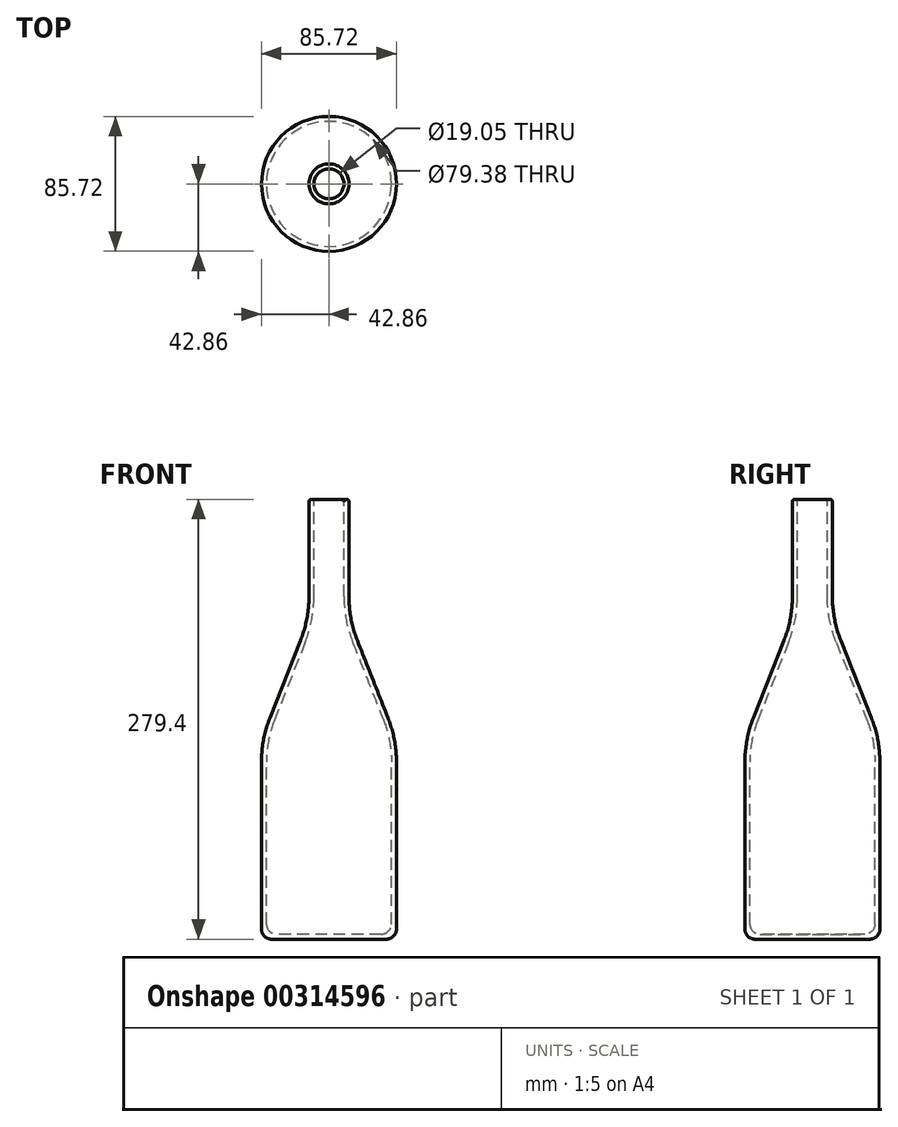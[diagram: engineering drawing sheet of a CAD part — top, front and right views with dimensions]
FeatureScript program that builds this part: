
annotation { "Feature Type Name" : "Feature", "Feature Type Description" : "" }
export const myFeature = defineFeature(function(context is Context, id is Id, definition is map)
    precondition{}
    {
        {
            var Q0;
            Q0=qCreatedBy(makeId("Front.planeOp"),FACE);
            var sketch = newSketch(context, id + "F0", { "sketchPlane" : qUnion([Q0])});
            skLineSegment(sketch, "E0", {"start": v(9.52, 152.56) * mm, "end": v(12.7, 152.56) * mm});
            skLineSegment(sketch, "E1", {"start": v(12.7, 152.56) * mm, "end": v(12.7, 90.9) * mm});
            skLineSegment(sketch, "E2", {"start": v(18.05, 62.85) * mm, "end": v(37.51, 13.67) * mm});
            skLineSegment(sketch, "E3", {"start": v(42.86, -14.37) * mm, "end": v(42.86, -120.49) * mm});
            skLineSegment(sketch, "E4", {"start": v(36.51, -126.84) * mm, "end": v(0, -126.84) * mm});
            skLineSegment(sketch, "E5", {"start": v(0, 152.56) * mm, "end": v(0, -126.84) * mm, "construction": true});
            skPoint(sketch, "E6.visualSharp", {"position": v(42.86, -126.84) * mm});
            skArc(sketch, "E6.filletArc", {"start": v(36.51, -126.84) * mm, "mid": v(41, -124.98) * mm, "end": v(42.86, -120.49) * mm});
            skPoint(sketch, "E7.visualSharp", {"position": v(42.86, 0.16) * mm});
            skArc(sketch, "E7.filletArc", {"start": v(42.86, -14.37) * mm, "mid": v(41.51, -0.1) * mm, "end": v(37.51, 13.67) * mm});
            skPoint(sketch, "E8.visualSharp", {"position": v(12.7, 76.36) * mm});
            skArc(sketch, "E8.filletArc", {"start": v(12.7, 90.9) * mm, "mid": v(14.05, 76.62) * mm, "end": v(18.05, 62.85) * mm});
            skLineSegment(sketch, "E9.0", {"start": v(33.34, -123.66) * mm, "end": v(0, -123.66) * mm});
            skLineSegment(sketch, "E9.1", {"start": v(39.69, -14.37) * mm, "end": v(39.69, -117.31) * mm});
            skLineSegment(sketch, "E9.2", {"start": v(9.52, 152.56) * mm, "end": v(9.52, 90.9) * mm});
            skArc(sketch, "E9.3", {"start": v(9.52, 90.9) * mm, "mid": v(10.93, 76.02) * mm, "end": v(15.1, 61.68) * mm});
            skLineSegment(sketch, "E9.4", {"start": v(15.1, 61.68) * mm, "end": v(34.56, 12.5) * mm});
            skArc(sketch, "E9.5", {"start": v(39.69, -14.37) * mm, "mid": v(38.4, -0.7) * mm, "end": v(34.56, 12.5) * mm});
            skPoint(sketch, "E10.visualSharp", {"position": v(39.69, -123.66) * mm});
            skArc(sketch, "E10.filletArc", {"start": v(33.34, -123.66) * mm, "mid": v(37.83, -121.8) * mm, "end": v(39.69, -117.31) * mm});
            skLineSegment(sketch, "E11", {"start": v(0, -123.66) * mm, "end": v(0, -126.84) * mm});
            skSolve(sketch);
        }
        {
            var Q0;
            Q0=makeQuery(id+"F0.imprint","IMPRINT",FACE,{"disambiguationData":[TD([[makeQuery(id+"F0.imprint","IMPRINT",EDGE,{"derivedFrom":sQuery(id+"F0.wireOp",EDGE,"E0")}),-1.0]])]});
            var Q1;
            Q1=sQuery(id+"F0.wireOp",EDGE,"E2");
            var Q2;
            Q2=sQuery(id+"F0.wireOp",EDGE,"E3");
            var Q3;
            Q3=sQuery(id+"F0.wireOp",EDGE,"E4");
            var Q4;
            Q4=sQuery(id+"F0.wireOp",EDGE,"E1");
            var Q5;
            Q5=sQuery(id+"F0.wireOp",EDGE,"E0");
            var Q6;
            Q6=sQuery(id+"F0.wireOp",EDGE,"E5");
            revolve(context, id + "F1", {"entities" : qUnion([Q0]), "surfaceEntities" : qUnion([Q1, Q2, Q3, Q4, Q5]), "axis" : qUnion([Q6]), "revolveType" : RevolveType.FULL});
        }
        {
            var Q0;
            Q0=makeQuery(id+"F1.opRevolve","SWEPT_EDGE",EDGE,{"disambiguationData":[OSD([sQuery(id+"F0.wireOp",EDGE,"E0"),sQuery(id+"F0.wireOp",EDGE,"E1")])]});
            var Q1;
            Q1=makeQuery(id+"F1.opRevolve","SWEPT_EDGE",EDGE,{"disambiguationData":[OSD([sQuery(id+"F0.wireOp",EDGE,"E0"),sQuery(id+"F0.wireOp",EDGE,"E9.2")])]});
            fillet(context, id + "F2", {"entities" : qUnion([Q0, Q1]), "radius" : 1.59 * mm, "tangentPropagation" : true, "allowEdgeOverflow" : false});
        }
    });
